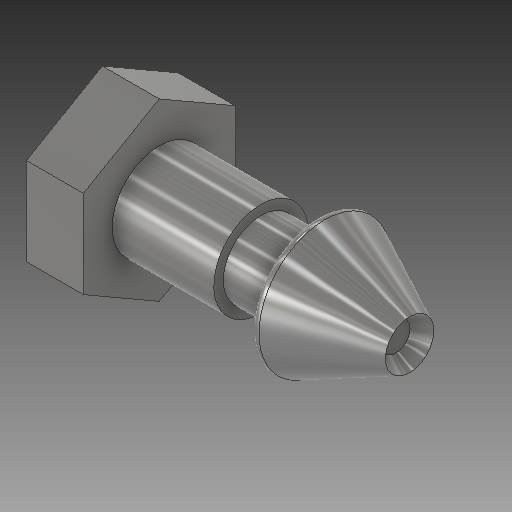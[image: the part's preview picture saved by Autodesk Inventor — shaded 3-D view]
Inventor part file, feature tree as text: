
AUTODESK INVENTOR PART (.ipt)
format: ipt  version: 2019 (Build 230136000, 136)  size: 202,240 bytes
history: native  units: mm
features: sketch x2, revolve x1, extrude x1, fillet x1
ambient origin geometry x8: Origin, YZ Plane, XZ Plane, XY Plane, X Axis, Y Axis, Z Axis, Center Point
bodies: Solid1 (feature_tree)
feature tree (5):
  revolve  "Revolution1"  [1 undecoded]
  extrude  "Extrusion1"  Depth=6.0mm
  fillet  "Fillet1"  Radius=5.116mm
  sketch  "Sketch1"  dims[d0=10.717mm d1=9.938mm]
  sketch  "Sketch2"  dims[d2=7.936mm d3=6.0mm d4=5.116mm d6=4.537856mm d7=90.0deg d8=9.67mm d9=6.283185mm d10=3.0mm d11=16.0mm d12=6.0mm d13=0.0mm d14=0.5mm]
note: 1 required parameter value undecoded (feature->parameter linkage not recoverable at this tier; creation-order binding heuristic only, values carry confidence <= 0.55)
